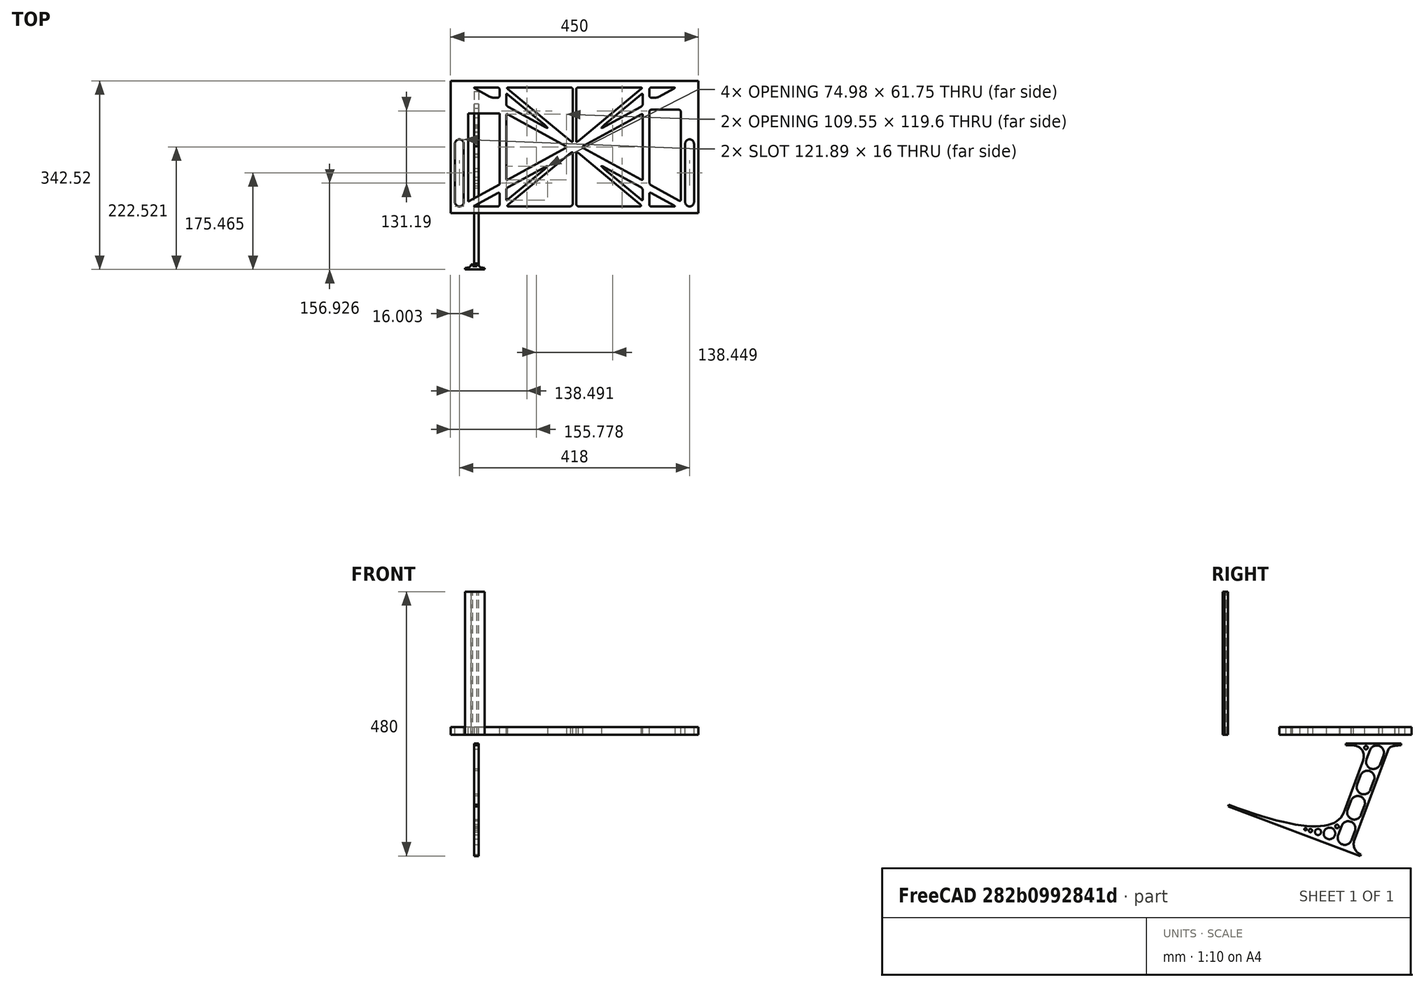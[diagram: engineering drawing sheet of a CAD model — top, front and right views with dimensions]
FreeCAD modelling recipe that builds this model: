
FCSTD DOCUMENT  (FreeCAD 0.19R0.19.2)
Label: laptopStand128FCStd
License: All rights reserved
LicenseURL: http://en.wikipedia.org/wiki/All_rights_reserved
objects: Sketcher::SketchObject×3, Part::Extrusion×3
note: 6 computed .brp shape members not serialized (recipe doc carries the construction recipe); baked Part::Feature solids carry a one-line shape summary decoded from their .brp

FEATURE [Sketcher::SketchObject] Sketch
  FullyConstrained = true
  sketch-geometry (353):
    g0: LineSegment StartX=-10.9272 StartY=-82.7794 StartZ=0 EndX=46.0728 EndY=-51.4823 EndZ=0
    g1: LineSegment StartX=-10.9272 StartY=76.4095 StartZ=0 EndX=-10.9272 EndY=-82.7794 EndZ=0
    g2: LineSegment StartX=46.0728 StartY=76.4095 StartZ=0 EndX=46.0728 EndY=-51.4823 EndZ=0
    g3: LineSegment StartX=-42.9272 StartY=136.221 StartZ=0 EndX=-42.9272 EndY=-103.779 EndZ=0
    g4: LineSegment StartX=407.073 StartY=136.221 StartZ=0 EndX=407.073 EndY=-103.779 EndZ=0
    g5: ArcOfCircle CenterX=-26.9272 CenterY=22.1087 CenterZ=0 NormalX=0 NormalY=0 NormalZ=1 AngleXU=0 Radius=8 StartAngle=1e-16 EndAngle=3.14159
    g6: ArcOfCircle CenterX=-26.9272 CenterY=-83.7794 CenterZ=0 NormalX=0 NormalY=0 NormalZ=1 AngleXU=0 Radius=8 StartAngle=3.14159 EndAngle=6.28319
    g7: LineSegment StartX=-34.9272 StartY=22.1087 StartZ=0 EndX=-34.9272 EndY=-83.7794 EndZ=0
    g8: LineSegment StartX=-18.9272 StartY=22.1087 StartZ=0 EndX=-18.9272 EndY=-83.7794 EndZ=0
    g9: ArcOfCircle CenterX=391.073 CenterY=22.1087 CenterZ=0 NormalX=0 NormalY=0 NormalZ=1 AngleXU=0 Radius=8 StartAngle=-4.4e-15 EndAngle=3.14159
    g10: LineSegment StartX=399.073 StartY=22.1087 StartZ=0 EndX=399.073 EndY=-83.7794 EndZ=0
    g11: LineSegment StartX=383.073 StartY=22.1087 StartZ=0 EndX=383.073 EndY=-83.7794 EndZ=0
    g12: ArcOfCircle CenterX=391.073 CenterY=-83.7794 CenterZ=0 NormalX=0 NormalY=0 NormalZ=1 AngleXU=0 Radius=8 StartAngle=3.14159 EndAngle=6.28319
    g13: Circle CenterX=175.022 CenterY=27.0628 CenterZ=0 NormalX=0 NormalY=0 NormalZ=1 AngleXU=0 Radius=1
    g14: Circle CenterX=179.022 CenterY=24.8665 CenterZ=0 NormalX=0 NormalY=0 NormalZ=1 AngleXU=0 Radius=1
    g15: Circle CenterX=179.022 CenterY=27.0628 CenterZ=0 NormalX=0 NormalY=0 NormalZ=1 AngleXU=0 Radius=1
    g16: BSplineCurve PolesCount=3 KnotsCount=2 Degree=2 IsPeriodic=0
    g17: GeomPoint X=175.022 Y=27.0628 Z=0
    g18: GeomPoint X=179.022 Y=27.0628 Z=0
    g19: Circle CenterX=189.124 CenterY=27.0628 CenterZ=0 NormalX=0 NormalY=0 NormalZ=1 AngleXU=0 Radius=1
    g20: Circle CenterX=185.124 CenterY=24.8665 CenterZ=0 NormalX=0 NormalY=0 NormalZ=1 AngleXU=0 Radius=1
    g21: Circle CenterX=185.124 CenterY=27.0628 CenterZ=0 NormalX=0 NormalY=0 NormalZ=1 AngleXU=0 Radius=1
    g22: BSplineCurve PolesCount=3 KnotsCount=2 Degree=2 IsPeriodic=0
    g23: GeomPoint X=189.124 Y=27.0628 Z=0
    g24: GeomPoint X=185.124 Y=27.0628 Z=0
    g25: Circle CenterX=175.022 CenterY=5.37834 CenterZ=0 NormalX=0 NormalY=0 NormalZ=1 AngleXU=0 Radius=1
    g26: Circle CenterX=179.022 CenterY=7.57463 CenterZ=0 NormalX=0 NormalY=0 NormalZ=1 AngleXU=0 Radius=1
    g27: Circle CenterX=179.022 CenterY=5.34704 CenterZ=0 NormalX=0 NormalY=0 NormalZ=1 AngleXU=0 Radius=1
    g28: BSplineCurve PolesCount=3 KnotsCount=2 Degree=2 IsPeriodic=0
    g29: GeomPoint X=175.022 Y=5.37834 Z=0
    g30: GeomPoint X=179.022 Y=5.34704 Z=0
    g31: Circle CenterX=189.124 CenterY=5.37834 CenterZ=0 NormalX=0 NormalY=0 NormalZ=1 AngleXU=0 Radius=1
    g32: Circle CenterX=185.124 CenterY=7.57463 CenterZ=0 NormalX=0 NormalY=0 NormalZ=1 AngleXU=0 Radius=1
    g33: Circle CenterX=185.124 CenterY=5.34704 CenterZ=0 NormalX=0 NormalY=0 NormalZ=1 AngleXU=0 Radius=1
    g34: BSplineCurve PolesCount=3 KnotsCount=2 Degree=2 IsPeriodic=0
    g35: GeomPoint X=189.124 Y=5.37834 Z=0
    g36: GeomPoint X=185.124 Y=5.34704 Z=0
    g37: Circle CenterX=165.871 CenterY=18.1458 CenterZ=0 NormalX=0 NormalY=0 NormalZ=1 AngleXU=0 Radius=1
    g38: Circle CenterX=169.377 CenterY=16.2206 CenterZ=0 NormalX=0 NormalY=0 NormalZ=1 AngleXU=0 Radius=1
    g39: Circle CenterX=165.871 CenterY=14.2954 CenterZ=0 NormalX=0 NormalY=0 NormalZ=1 AngleXU=0 Radius=1
    g40: BSplineCurve PolesCount=3 KnotsCount=2 Degree=2 IsPeriodic=0
    g41: GeomPoint X=165.871 Y=18.1458 Z=0
    g42: GeomPoint X=165.871 Y=14.2954 Z=0
    g43: Circle CenterX=198.275 CenterY=18.1458 CenterZ=0 NormalX=0 NormalY=0 NormalZ=1 AngleXU=0 Radius=1
    g44: Circle CenterX=194.768 CenterY=16.2206 CenterZ=0 NormalX=0 NormalY=0 NormalZ=1 AngleXU=0 Radius=1
    g45: Circle CenterX=198.275 CenterY=14.2954 CenterZ=0 NormalX=0 NormalY=0 NormalZ=1 AngleXU=0 Radius=1
    g46: BSplineCurve PolesCount=3 KnotsCount=2 Degree=2 IsPeriodic=0
    g47: GeomPoint X=198.275 Y=18.1458 Z=0
    g48: GeomPoint X=198.275 Y=14.2954 Z=0
    g49: LineSegment StartX=407.073 StartY=-103.779 StartZ=0 EndX=-42.9272 EndY=-103.779 EndZ=0
    g50: LineSegment StartX=407.073 StartY=136.221 StartZ=0 EndX=-42.9272 EndY=136.221 EndZ=0
    g51: LineSegment StartX=46.0728 StartY=76.4095 StartZ=0 EndX=-10.9272 EndY=76.4095 EndZ=0
    g52: Circle CenterX=125.607 CenterY=54.1951 CenterZ=0 NormalX=0 NormalY=0 NormalZ=1 AngleXU=0 Radius=1
    g53: Circle CenterX=139.632 CenterY=46.4944 CenterZ=0 NormalX=0 NormalY=0 NormalZ=1 AngleXU=0 Radius=1
    g54: Circle CenterX=127.326 CenterY=56.7187 CenterZ=0 NormalX=0 NormalY=0 NormalZ=1 AngleXU=0 Radius=1
    g55: BSplineCurve PolesCount=3 KnotsCount=2 Degree=2 IsPeriodic=0
    g56: GeomPoint X=125.607 Y=54.1951 Z=0
    g57: GeomPoint X=127.326 Y=56.7187 Z=0
    g58: Circle CenterX=236.821 CenterY=56.7187 CenterZ=0 NormalX=0 NormalY=0 NormalZ=1 AngleXU=0 Radius=1
    g59: Circle CenterX=224.513 CenterY=46.4944 CenterZ=0 NormalX=0 NormalY=0 NormalZ=1 AngleXU=0 Radius=1
    g60: Circle CenterX=238.538 CenterY=54.1951 CenterZ=0 NormalX=0 NormalY=0 NormalZ=1 AngleXU=0 Radius=1
    g61: BSplineCurve PolesCount=3 KnotsCount=2 Degree=2 IsPeriodic=0
    g62: GeomPoint X=236.821 Y=56.7187 Z=0
    g63: GeomPoint X=238.538 Y=54.1951 Z=0
    g64: Circle CenterX=238.538 CenterY=-21.7539 CenterZ=0 NormalX=0 NormalY=0 NormalZ=1 AngleXU=0 Radius=1
    g65: Circle CenterX=224.513 CenterY=-14.0532 CenterZ=0 NormalX=0 NormalY=0 NormalZ=1 AngleXU=0 Radius=1
    g66: Circle CenterX=236.821 CenterY=-24.2775 CenterZ=0 NormalX=0 NormalY=0 NormalZ=1 AngleXU=0 Radius=1
    g67: BSplineCurve PolesCount=3 KnotsCount=2 Degree=2 IsPeriodic=0
    g68: GeomPoint X=238.538 Y=-21.7539 Z=0
    g69: GeomPoint X=236.821 Y=-24.2775 Z=0
    g70: Circle CenterX=125.607 CenterY=-21.7539 CenterZ=0 NormalX=0 NormalY=0 NormalZ=1 AngleXU=0 Radius=1
    g71: Circle CenterX=139.632 CenterY=-14.0532 CenterZ=0 NormalX=0 NormalY=0 NormalZ=1 AngleXU=0 Radius=1
    g72: Circle CenterX=127.325 CenterY=-24.2775 CenterZ=0 NormalX=0 NormalY=0 NormalZ=1 AngleXU=0 Radius=1
    g73: BSplineCurve PolesCount=3 KnotsCount=2 Degree=2 IsPeriodic=0
    g74: GeomPoint X=125.607 Y=-21.7539 Z=0
    g75: GeomPoint X=127.325 Y=-24.2775 Z=0
    g76: Circle CenterX=302.996 CenterY=111.695 CenterZ=0 NormalX=0 NormalY=0 NormalZ=1 AngleXU=0 Radius=1
    g77: Circle CenterX=306.073 CenterY=114.251 CenterZ=0 NormalX=0 NormalY=0 NormalZ=1 AngleXU=0 Radius=1
    g78: Circle CenterX=306.073 CenterY=110.251 CenterZ=0 NormalX=0 NormalY=0 NormalZ=1 AngleXU=0 Radius=1
    g79: BSplineCurve PolesCount=3 KnotsCount=2 Degree=2 IsPeriodic=0
    g80: GeomPoint X=302.996 Y=111.695 Z=0
    g81: GeomPoint X=306.073 Y=110.251 Z=0
    g82: Circle CenterX=306.073 CenterY=95.2763 CenterZ=0 NormalX=0 NormalY=0 NormalZ=1 AngleXU=0 Radius=1
    g83: Circle CenterX=306.073 CenterY=91.2763 CenterZ=0 NormalX=0 NormalY=0 NormalZ=1 AngleXU=0 Radius=1
    g84: Circle CenterX=302.567 CenterY=89.3511 CenterZ=0 NormalX=0 NormalY=0 NormalZ=1 AngleXU=0 Radius=1
    g85: BSplineCurve PolesCount=3 KnotsCount=2 Degree=2 IsPeriodic=0
    g86: GeomPoint X=306.073 Y=95.2763 Z=0
    g87: GeomPoint X=302.567 Y=89.3511 Z=0
    g88: LineSegment StartX=306.073 StartY=110.251 StartZ=0 EndX=306.073 EndY=95.2763 EndZ=0
    g89: LineSegment StartX=302.996 StartY=111.695 StartZ=0 EndX=236.821 EndY=56.7187 EndZ=0
    g90: LineSegment StartX=238.538 StartY=54.1951 StartZ=0 EndX=302.567 EndY=89.3511 EndZ=0
    g91: Circle CenterX=61.1496 CenterY=111.695 CenterZ=0 NormalX=0 NormalY=0 NormalZ=1 AngleXU=0 Radius=1
    g92: Circle CenterX=58.0728 CenterY=114.251 CenterZ=0 NormalX=0 NormalY=0 NormalZ=1 AngleXU=0 Radius=1
    g93: Circle CenterX=58.0728 CenterY=110.251 CenterZ=0 NormalX=0 NormalY=0 NormalZ=1 AngleXU=0 Radius=1
    g94: BSplineCurve PolesCount=3 KnotsCount=2 Degree=2 IsPeriodic=0
    g95: GeomPoint X=61.1496 Y=111.695 Z=0
    g96: GeomPoint X=58.0728 Y=110.251 Z=0
    g97: Circle CenterX=61.5791 CenterY=89.3511 CenterZ=0 NormalX=0 NormalY=0 NormalZ=1 AngleXU=0 Radius=1
    g98: Circle CenterX=58.0728 CenterY=91.2763 CenterZ=0 NormalX=0 NormalY=0 NormalZ=1 AngleXU=0 Radius=1
    g99: Circle CenterX=58.0728 CenterY=95.2763 CenterZ=0 NormalX=0 NormalY=0 NormalZ=1 AngleXU=0 Radius=1
    g100: BSplineCurve PolesCount=3 KnotsCount=2 Degree=2 IsPeriodic=0
    g101: GeomPoint X=61.5791 Y=89.3511 Z=0
    g102: GeomPoint X=58.0728 Y=95.2763 Z=0
    g103: LineSegment StartX=58.0728 StartY=110.251 StartZ=0 EndX=58.0728 EndY=95.2763 EndZ=0
    g104: LineSegment StartX=61.1496 StartY=111.695 StartZ=0 EndX=127.326 EndY=56.7187 EndZ=0
    g105: LineSegment StartX=125.607 StartY=54.1951 StartZ=0 EndX=61.5791 EndY=89.3511 EndZ=0
    g106: Circle CenterX=61.5791 CenterY=-56.9099 CenterZ=0 NormalX=0 NormalY=0 NormalZ=1 AngleXU=0 Radius=1
    g107: Circle CenterX=58.0728 CenterY=-58.8351 CenterZ=0 NormalX=0 NormalY=0 NormalZ=1 AngleXU=0 Radius=1
    g108: Circle CenterX=58.0728 CenterY=-62.8351 CenterZ=0 NormalX=0 NormalY=0 NormalZ=1 AngleXU=0 Radius=1
    g109: BSplineCurve PolesCount=3 KnotsCount=2 Degree=2 IsPeriodic=0
    g110: GeomPoint X=61.5791 Y=-56.9099 Z=0
    g111: GeomPoint X=58.0728 Y=-62.8351 Z=0
    g112: Circle CenterX=58.0728 CenterY=-77.8102 CenterZ=0 NormalX=0 NormalY=0 NormalZ=1 AngleXU=0 Radius=1
    g113: Circle CenterX=58.0728 CenterY=-81.8102 CenterZ=0 NormalX=0 NormalY=0 NormalZ=1 AngleXU=0 Radius=1
    g114: Circle CenterX=61.1496 CenterY=-79.2541 CenterZ=0 NormalX=0 NormalY=0 NormalZ=1 AngleXU=0 Radius=1
    g115: BSplineCurve PolesCount=3 KnotsCount=2 Degree=2 IsPeriodic=0
    g116: GeomPoint X=58.0728 Y=-77.8102 Z=0
    g117: GeomPoint X=61.1496 Y=-79.2541 Z=0
    g118: LineSegment StartX=58.0728 StartY=-62.8351 StartZ=0 EndX=58.0728 EndY=-77.8102 EndZ=0
    g119: LineSegment StartX=61.1496 StartY=-79.2541 StartZ=0 EndX=127.325 EndY=-24.2775 EndZ=0
    g120: LineSegment StartX=125.607 StartY=-21.7539 StartZ=0 EndX=61.5791 EndY=-56.9099 EndZ=0
    g121: Circle CenterX=302.567 CenterY=-56.9099 CenterZ=0 NormalX=0 NormalY=0 NormalZ=1 AngleXU=0 Radius=1
    g122: Circle CenterX=306.073 CenterY=-58.8351 CenterZ=0 NormalX=0 NormalY=0 NormalZ=1 AngleXU=0 Radius=1
    g123: Circle CenterX=306.073 CenterY=-62.8351 CenterZ=0 NormalX=0 NormalY=0 NormalZ=1 AngleXU=0 Radius=1
    g124: BSplineCurve PolesCount=3 KnotsCount=2 Degree=2 IsPeriodic=0
    g125: GeomPoint X=302.567 Y=-56.9099 Z=0
    g126: GeomPoint X=306.073 Y=-62.8351 Z=0
    g127: Circle CenterX=302.996 CenterY=-79.2541 CenterZ=0 NormalX=0 NormalY=0 NormalZ=1 AngleXU=0 Radius=1
    g128: Circle CenterX=306.073 CenterY=-81.8102 CenterZ=0 NormalX=0 NormalY=0 NormalZ=1 AngleXU=0 Radius=1
    g129: Circle CenterX=306.073 CenterY=-77.8102 CenterZ=0 NormalX=0 NormalY=0 NormalZ=1 AngleXU=0 Radius=1
    g130: BSplineCurve PolesCount=3 KnotsCount=2 Degree=2 IsPeriodic=0
    g131: GeomPoint X=302.996 Y=-79.2541 Z=0
    g132: GeomPoint X=306.073 Y=-77.8102 Z=0
    g133: LineSegment StartX=306.073 StartY=-62.8351 StartZ=0 EndX=306.073 EndY=-77.8102 EndZ=0
    g134: LineSegment StartX=302.996 StartY=-79.2541 StartZ=0 EndX=236.821 EndY=-24.2775 EndZ=0
    g135: LineSegment StartX=238.538 StartY=-21.7539 StartZ=0 EndX=302.567 EndY=-56.9099 EndZ=0
    g136: Circle CenterX=61.6457 CenterY=-88.8112 CenterZ=0 NormalX=0 NormalY=0 NormalZ=1 AngleXU=0 Radius=1
    g137: Circle CenterX=58.0728 CenterY=-91.7794 CenterZ=0 NormalX=0 NormalY=0 NormalZ=1 AngleXU=0 Radius=1
    g138: Circle CenterX=63.9135 CenterY=-91.7794 CenterZ=0 NormalX=0 NormalY=0 NormalZ=1 AngleXU=0 Radius=1
    g139: BSplineCurve PolesCount=3 KnotsCount=2 Degree=2 IsPeriodic=0
    g140: GeomPoint X=61.6457 Y=-88.8112 Z=0
    g141: GeomPoint X=63.9135 Y=-91.7794 Z=0
    g142: Circle CenterX=179.022 CenterY=-85.8163 CenterZ=0 NormalX=0 NormalY=0 NormalZ=1 AngleXU=0 Radius=1
    g143: Circle CenterX=179.022 CenterY=-91.7794 CenterZ=0 NormalX=0 NormalY=0 NormalZ=1 AngleXU=0 Radius=1
    g144: Circle CenterX=171.895 CenterY=-91.7794 CenterZ=0 NormalX=0 NormalY=0 NormalZ=1 AngleXU=0 Radius=1
    g145: BSplineCurve PolesCount=3 KnotsCount=2 Degree=2 IsPeriodic=0
    g146: GeomPoint X=179.022 Y=-85.8163 Z=0
    g147: GeomPoint X=171.895 Y=-91.7794 Z=0
    g148: Circle CenterX=185.124 CenterY=-86.2028 CenterZ=0 NormalX=0 NormalY=0 NormalZ=1 AngleXU=0 Radius=1
    g149: Circle CenterX=185.124 CenterY=-91.7794 CenterZ=0 NormalX=0 NormalY=0 NormalZ=1 AngleXU=0 Radius=1
    g150: Circle CenterX=191.747 CenterY=-91.7794 CenterZ=0 NormalX=0 NormalY=0 NormalZ=1 AngleXU=0 Radius=1
    g151: BSplineCurve PolesCount=3 KnotsCount=2 Degree=2 IsPeriodic=0
    g152: GeomPoint X=185.124 Y=-86.2028 Z=0
    g153: GeomPoint X=191.747 Y=-91.7794 Z=0
    g154: Circle CenterX=299.888 CenterY=-86.6413 CenterZ=0 NormalX=0 NormalY=0 NormalZ=1 AngleXU=0 Radius=1
    g155: Circle CenterX=306.073 CenterY=-91.7794 CenterZ=0 NormalX=0 NormalY=0 NormalZ=1 AngleXU=0 Radius=1
    g156: Circle CenterX=298.776 CenterY=-91.7794 CenterZ=0 NormalX=0 NormalY=0 NormalZ=1 AngleXU=0 Radius=1
    g157: BSplineCurve PolesCount=3 KnotsCount=2 Degree=2 IsPeriodic=0
    g158: GeomPoint X=299.888 Y=-86.6413 Z=0
    g159: GeomPoint X=298.776 Y=-91.7794 Z=0
    g160: LineSegment StartX=189.124 StartY=5.37834 StartZ=0 EndX=299.888 EndY=-86.6413 EndZ=0
    g161: LineSegment StartX=298.776 StartY=-91.7794 StartZ=0 EndX=191.747 EndY=-91.7794 EndZ=0
    g162: LineSegment StartX=185.124 StartY=-86.2028 StartZ=0 EndX=185.124 EndY=5.34704 EndZ=0
    g163: LineSegment StartX=179.022 StartY=5.34704 StartZ=0 EndX=179.022 EndY=-85.8163 EndZ=0
    g164: LineSegment StartX=171.895 StartY=-91.7794 StartZ=0 EndX=63.9135 EndY=-91.7794 EndZ=0
    g165: LineSegment StartX=61.6457 StartY=-88.8112 StartZ=0 EndX=175.022 EndY=5.37834 EndZ=0
    g166: Circle CenterX=302.073 CenterY=124.221 CenterZ=0 NormalX=0 NormalY=0 NormalZ=1 AngleXU=0 Radius=1
    g167: Circle CenterX=306.073 CenterY=124.221 CenterZ=0 NormalX=0 NormalY=0 NormalZ=1 AngleXU=0 Radius=1
    g168: Circle CenterX=302.996 CenterY=121.665 CenterZ=0 NormalX=0 NormalY=0 NormalZ=1 AngleXU=0 Radius=1
    g169: BSplineCurve PolesCount=3 KnotsCount=2 Degree=2 IsPeriodic=0
    g170: GeomPoint X=302.073 Y=124.221 Z=0
    g171: GeomPoint X=302.996 Y=121.665 Z=0
    g172: Circle CenterX=189.124 CenterY=124.221 CenterZ=0 NormalX=0 NormalY=0 NormalZ=1 AngleXU=0 Radius=1
    g173: Circle CenterX=185.124 CenterY=124.221 CenterZ=0 NormalX=0 NormalY=0 NormalZ=1 AngleXU=0 Radius=1
    g174: Circle CenterX=185.124 CenterY=120.221 CenterZ=0 NormalX=0 NormalY=0 NormalZ=1 AngleXU=0 Radius=1
    g175: BSplineCurve PolesCount=3 KnotsCount=2 Degree=2 IsPeriodic=0
    g176: GeomPoint X=189.124 Y=124.221 Z=0
    g177: GeomPoint X=185.124 Y=120.221 Z=0
    g178: Circle CenterX=175.022 CenterY=124.221 CenterZ=0 NormalX=0 NormalY=0 NormalZ=1 AngleXU=0 Radius=1
    g179: Circle CenterX=179.022 CenterY=124.221 CenterZ=0 NormalX=0 NormalY=0 NormalZ=1 AngleXU=0 Radius=1
    g180: Circle CenterX=179.022 CenterY=120.221 CenterZ=0 NormalX=0 NormalY=0 NormalZ=1 AngleXU=0 Radius=1
    g181: BSplineCurve PolesCount=3 KnotsCount=2 Degree=2 IsPeriodic=0
    g182: GeomPoint X=175.022 Y=124.221 Z=0
    g183: GeomPoint X=179.022 Y=120.221 Z=0
    g184: Circle CenterX=62.0728 CenterY=124.221 CenterZ=0 NormalX=0 NormalY=0 NormalZ=1 AngleXU=0 Radius=1
    g185: Circle CenterX=58.0728 CenterY=124.221 CenterZ=0 NormalX=0 NormalY=0 NormalZ=1 AngleXU=0 Radius=1
    g186: Circle CenterX=61.1496 CenterY=121.665 CenterZ=0 NormalX=0 NormalY=0 NormalZ=1 AngleXU=0 Radius=1
    g187: BSplineCurve PolesCount=3 KnotsCount=2 Degree=2 IsPeriodic=0
    g188: GeomPoint X=62.0728 Y=124.221 Z=0
    g189: GeomPoint X=61.1496 Y=121.665 Z=0
    g190: LineSegment StartX=62.0728 StartY=124.221 StartZ=0 EndX=175.022 EndY=124.221 EndZ=0
    g191: LineSegment StartX=179.022 StartY=120.221 StartZ=0 EndX=179.022 EndY=27.0628 EndZ=0
    g192: LineSegment StartX=185.124 StartY=27.0628 StartZ=0 EndX=185.124 EndY=120.221 EndZ=0
    g193: LineSegment StartX=189.124 StartY=124.221 StartZ=0 EndX=302.073 EndY=124.221 EndZ=0
    g194: LineSegment StartX=302.996 StartY=121.665 StartZ=0 EndX=189.124 EndY=27.0628 EndZ=0
    g195: LineSegment StartX=175.022 StartY=27.0628 StartZ=0 EndX=61.1496 EndY=121.665 EndZ=0
    g196: Circle CenterX=61.5791 CenterY=75.4095 CenterZ=0 NormalX=0 NormalY=0 NormalZ=1 AngleXU=0 Radius=1
    g197: Circle CenterX=58.0728 CenterY=77.3346 CenterZ=0 NormalX=0 NormalY=0 NormalZ=1 AngleXU=0 Radius=1
    g198: Circle CenterX=58.0728 CenterY=73.3346 CenterZ=0 NormalX=0 NormalY=0 NormalZ=1 AngleXU=0 Radius=1
    g199: BSplineCurve PolesCount=3 KnotsCount=2 Degree=2 IsPeriodic=0
    g200: GeomPoint X=61.5791 Y=75.4095 Z=0
    g201: GeomPoint X=58.0728 Y=73.3346 Z=0
    g202: Circle CenterX=58.0728 CenterY=-40.8935 CenterZ=0 NormalX=0 NormalY=0 NormalZ=1 AngleXU=0 Radius=1
    g203: Circle CenterX=58.0728 CenterY=-44.8935 CenterZ=0 NormalX=0 NormalY=0 NormalZ=1 AngleXU=0 Radius=1
    g204: Circle CenterX=61.5791 CenterY=-42.9683 CenterZ=0 NormalX=0 NormalY=0 NormalZ=1 AngleXU=0 Radius=1
    g205: BSplineCurve PolesCount=3 KnotsCount=2 Degree=2 IsPeriodic=0
    g206: GeomPoint X=58.0728 Y=-40.8935 Z=0
    g207: GeomPoint X=61.5791 Y=-42.9683 Z=0
    g208: LineSegment StartX=61.5791 StartY=-42.9683 StartZ=0 EndX=165.871 EndY=14.2954 EndZ=0
    g209: LineSegment StartX=165.871 StartY=18.1458 StartZ=0 EndX=61.5791 EndY=75.4095 EndZ=0
    g210: LineSegment StartX=58.0728 StartY=73.3346 StartZ=0 EndX=58.0728 EndY=-40.8935 EndZ=0
    g211: Circle CenterX=302.567 CenterY=-42.9683 CenterZ=0 NormalX=0 NormalY=0 NormalZ=1 AngleXU=0 Radius=1
    g212: Circle CenterX=306.073 CenterY=-44.8935 CenterZ=0 NormalX=0 NormalY=0 NormalZ=1 AngleXU=0 Radius=1
    g213: Circle CenterX=306.073 CenterY=-40.8935 CenterZ=0 NormalX=0 NormalY=0 NormalZ=1 AngleXU=0 Radius=1
    g214: BSplineCurve PolesCount=3 KnotsCount=2 Degree=2 IsPeriodic=0
    g215: GeomPoint X=302.567 Y=-42.9683 Z=0
    g216: GeomPoint X=306.073 Y=-40.8935 Z=0
    g217: Circle CenterX=306.073 CenterY=73.3346 CenterZ=0 NormalX=0 NormalY=0 NormalZ=1 AngleXU=0 Radius=1
    g218: Circle CenterX=306.073 CenterY=77.3346 CenterZ=0 NormalX=0 NormalY=0 NormalZ=1 AngleXU=0 Radius=1
    g219: Circle CenterX=302.567 CenterY=75.4095 CenterZ=0 NormalX=0 NormalY=0 NormalZ=1 AngleXU=0 Radius=1
    g220: BSplineCurve PolesCount=3 KnotsCount=2 Degree=2 IsPeriodic=0
    g221: GeomPoint X=306.073 Y=73.3346 Z=0
    g222: GeomPoint X=302.567 Y=75.4095 Z=0
    g223: LineSegment StartX=302.567 StartY=-42.9683 StartZ=0 EndX=198.275 EndY=14.2954 EndZ=0
    g224: LineSegment StartX=198.275 StartY=18.1458 StartZ=0 EndX=302.567 EndY=75.4095 EndZ=0
    g225: LineSegment StartX=306.073 StartY=73.3346 StartZ=0 EndX=306.073 EndY=-40.8935 EndZ=0
    g226: LineSegment StartX=322.073 StartY=105.865 StartZ=0 EndX=328.643 EndY=105.865 EndZ=0
    g227: LineSegment StartX=318.073 StartY=120.221 StartZ=0 EndX=318.073 EndY=109.865 EndZ=0
    g228: LineSegment StartX=336.157 StartY=107.779 StartZ=0 EndX=362.567 EndY=122.294 EndZ=0
    g229: Circle CenterX=362.073 CenterY=124.221 CenterZ=0 NormalX=0 NormalY=0 NormalZ=1 AngleXU=0 Radius=1
    g230: Circle CenterX=366.073 CenterY=124.221 CenterZ=0 NormalX=0 NormalY=0 NormalZ=1 AngleXU=0 Radius=1
    g231: Circle CenterX=362.567 CenterY=122.294 CenterZ=0 NormalX=0 NormalY=0 NormalZ=1 AngleXU=0 Radius=1
    g232: BSplineCurve PolesCount=3 KnotsCount=2 Degree=2 IsPeriodic=0
    g233: GeomPoint X=362.073 Y=124.221 Z=0
    g234: GeomPoint X=362.567 Y=122.294 Z=0
    g235: Circle CenterX=322.073 CenterY=124.221 CenterZ=0 NormalX=0 NormalY=0 NormalZ=1 AngleXU=0 Radius=1
    g236: Circle CenterX=318.073 CenterY=124.221 CenterZ=0 NormalX=0 NormalY=0 NormalZ=1 AngleXU=0 Radius=1
    g237: Circle CenterX=318.073 CenterY=120.221 CenterZ=0 NormalX=0 NormalY=0 NormalZ=1 AngleXU=0 Radius=1
    g238: BSplineCurve PolesCount=3 KnotsCount=2 Degree=2 IsPeriodic=0
    g239: GeomPoint X=322.073 Y=124.221 Z=0
    g240: GeomPoint X=318.073 Y=120.221 Z=0
    g241: Circle CenterX=322.073 CenterY=105.865 CenterZ=0 NormalX=0 NormalY=0 NormalZ=1 AngleXU=0 Radius=1
    g242: Circle CenterX=318.073 CenterY=105.865 CenterZ=0 NormalX=0 NormalY=0 NormalZ=1 AngleXU=0 Radius=1
    g243: Circle CenterX=318.073 CenterY=109.865 CenterZ=0 NormalX=0 NormalY=0 NormalZ=1 AngleXU=0 Radius=1
    g244: BSplineCurve PolesCount=3 KnotsCount=2 Degree=2 IsPeriodic=0
    g245: GeomPoint X=322.073 Y=105.865 Z=0
    g246: GeomPoint X=318.073 Y=109.865 Z=0
    g247: Circle CenterX=336.157 CenterY=107.779 CenterZ=0 NormalX=0 NormalY=0 NormalZ=1 AngleXU=0 Radius=1
    g248: Circle CenterX=332.651 CenterY=105.853 CenterZ=0 NormalX=0 NormalY=0 NormalZ=1 AngleXU=0 Radius=1
    g249: Circle CenterX=328.643 CenterY=105.865 CenterZ=0 NormalX=0 NormalY=0 NormalZ=1 AngleXU=0 Radius=1
    g250: BSplineCurve PolesCount=3 KnotsCount=2 Degree=2 IsPeriodic=0
    g251: GeomPoint X=336.157 Y=107.779 Z=0
    g252: GeomPoint X=328.643 Y=105.865 Z=0
    g253: LineSegment StartX=322.073 StartY=124.221 StartZ=0 EndX=362.073 EndY=124.221 EndZ=0
    g254: Circle CenterX=371.567 CenterY=-80.8644 CenterZ=0 NormalX=0 NormalY=0 NormalZ=1 AngleXU=0 Radius=1
    g255: Circle CenterX=375.073 CenterY=-82.7896 CenterZ=0 NormalX=0 NormalY=0 NormalZ=1 AngleXU=0 Radius=1
    g256: Circle CenterX=375.073 CenterY=-78.7896 CenterZ=0 NormalX=0 NormalY=0 NormalZ=1 AngleXU=0 Radius=1
    g257: BSplineCurve PolesCount=3 KnotsCount=2 Degree=2 IsPeriodic=0
    g258: GeomPoint X=371.567 Y=-80.8644 Z=0
    g259: GeomPoint X=375.073 Y=-78.7896 Z=0
    g260: Circle CenterX=321.579 CenterY=-53.4075 CenterZ=0 NormalX=0 NormalY=0 NormalZ=1 AngleXU=0 Radius=1
    g261: Circle CenterX=318.073 CenterY=-51.4823 CenterZ=0 NormalX=0 NormalY=0 NormalZ=1 AngleXU=0 Radius=1
    g262: Circle CenterX=318.073 CenterY=-47.4823 CenterZ=0 NormalX=0 NormalY=0 NormalZ=1 AngleXU=0 Radius=1
    g263: BSplineCurve PolesCount=3 KnotsCount=2 Degree=2 IsPeriodic=0
    g264: GeomPoint X=321.579 Y=-53.4075 Z=0
    g265: GeomPoint X=318.073 Y=-47.4823 Z=0
    g266: Circle CenterX=318.073 CenterY=79.9235 CenterZ=0 NormalX=0 NormalY=0 NormalZ=1 AngleXU=0 Radius=1
    g267: Circle CenterX=318.073 CenterY=83.9235 CenterZ=0 NormalX=0 NormalY=0 NormalZ=1 AngleXU=0 Radius=1
    g268: Circle CenterX=322.073 CenterY=83.9235 CenterZ=0 NormalX=0 NormalY=0 NormalZ=1 AngleXU=0 Radius=1
    g269: BSplineCurve PolesCount=3 KnotsCount=2 Degree=2 IsPeriodic=0
    g270: GeomPoint X=318.073 Y=79.9235 Z=0
    g271: GeomPoint X=322.073 Y=83.9235 Z=0
    g272: Circle CenterX=375.073 CenterY=79.9235 CenterZ=0 NormalX=0 NormalY=0 NormalZ=1 AngleXU=0 Radius=1
    g273: Circle CenterX=375.073 CenterY=83.9235 CenterZ=0 NormalX=0 NormalY=0 NormalZ=1 AngleXU=0 Radius=1
    g274: Circle CenterX=371.073 CenterY=83.9235 CenterZ=0 NormalX=0 NormalY=0 NormalZ=1 AngleXU=0 Radius=1
    g275: BSplineCurve PolesCount=3 KnotsCount=2 Degree=2 IsPeriodic=0
    g276: GeomPoint X=375.073 Y=79.9235 Z=0
    g277: GeomPoint X=371.073 Y=83.9235 Z=0
    g278: LineSegment StartX=375.073 StartY=79.9235 StartZ=0 EndX=375.073 EndY=78.9235 EndZ=0
    g279: LineSegment StartX=371.567 StartY=-80.8644 StartZ=0 EndX=321.579 EndY=-53.4075 EndZ=0
    g280: LineSegment StartX=318.073 StartY=-47.4823 StartZ=0 EndX=318.073 EndY=76.4095 EndZ=0
    g281: Circle CenterX=321.579 CenterY=-67.3492 CenterZ=0 NormalX=0 NormalY=0 NormalZ=1 AngleXU=0 Radius=1
    g282: Circle CenterX=318.073 CenterY=-65.424 CenterZ=0 NormalX=0 NormalY=0 NormalZ=1 AngleXU=0 Radius=1
    g283: Circle CenterX=318.073 CenterY=-69.424 CenterZ=0 NormalX=0 NormalY=0 NormalZ=1 AngleXU=0 Radius=1
    g284: BSplineCurve PolesCount=3 KnotsCount=2 Degree=2 IsPeriodic=0
    g285: GeomPoint X=321.579 Y=-67.3492 Z=0
    g286: GeomPoint X=318.073 Y=-69.424 Z=0
    g287: Circle CenterX=362.567 CenterY=-89.8542 CenterZ=0 NormalX=0 NormalY=0 NormalZ=1 AngleXU=0 Radius=1
    g288: Circle CenterX=366.073 CenterY=-91.7794 CenterZ=0 NormalX=0 NormalY=0 NormalZ=1 AngleXU=0 Radius=1
    g289: Circle CenterX=362.073 CenterY=-91.7794 CenterZ=0 NormalX=0 NormalY=0 NormalZ=1 AngleXU=0 Radius=1
    g290: BSplineCurve PolesCount=3 KnotsCount=2 Degree=2 IsPeriodic=0
    g291: GeomPoint X=362.567 Y=-89.8542 Z=0
    g292: GeomPoint X=362.073 Y=-91.7794 Z=0
    g293: Circle CenterX=322.073 CenterY=-91.7794 CenterZ=0 NormalX=0 NormalY=0 NormalZ=1 AngleXU=0 Radius=1
    g294: Circle CenterX=318.073 CenterY=-91.7794 CenterZ=0 NormalX=0 NormalY=0 NormalZ=1 AngleXU=0 Radius=1
    g295: Circle CenterX=318.073 CenterY=-87.7794 CenterZ=0 NormalX=0 NormalY=0 NormalZ=1 AngleXU=0 Radius=1
    g296: BSplineCurve PolesCount=3 KnotsCount=2 Degree=2 IsPeriodic=0
    g297: GeomPoint X=322.073 Y=-91.7794 Z=0
    g298: GeomPoint X=318.073 Y=-87.7794 Z=0
    g299: LineSegment StartX=362.567 StartY=-89.8542 StartZ=0 EndX=321.579 EndY=-67.3492 EndZ=0
    g300: LineSegment StartX=318.073 StartY=-69.424 StartZ=0 EndX=318.073 EndY=-87.7794 EndZ=0
    g301: LineSegment StartX=322.073 StartY=-91.7794 StartZ=0 EndX=362.073 EndY=-91.7794 EndZ=0
    g302: Circle CenterX=2.07281 CenterY=124.221 CenterZ=0 NormalX=0 NormalY=0 NormalZ=1 AngleXU=0 Radius=1
    g303: Circle CenterX=1.57905 CenterY=122.295 CenterZ=0 NormalX=0 NormalY=0 NormalZ=1 AngleXU=0 Radius=1
    g304: BSplineCurve PolesCount=3 KnotsCount=2 Degree=2 IsPeriodic=0
    g305: GeomPoint X=2.07281 Y=124.221 Z=0
    g306: GeomPoint X=1.57905 Y=122.295 Z=0
    g307: Circle CenterX=42.0728 CenterY=124.221 CenterZ=0 NormalX=0 NormalY=0 NormalZ=1 AngleXU=0 Radius=1
    g308: Circle CenterX=46.0728 CenterY=124.221 CenterZ=0 NormalX=0 NormalY=0 NormalZ=1 AngleXU=0 Radius=1
    g309: Circle CenterX=46.0728 CenterY=120.221 CenterZ=0 NormalX=0 NormalY=0 NormalZ=1 AngleXU=0 Radius=1
    g310: BSplineCurve PolesCount=3 KnotsCount=2 Degree=2 IsPeriodic=0
    g311: GeomPoint X=42.0728 Y=124.221 Z=0
    g312: GeomPoint X=46.0728 Y=120.221 Z=0
    g313: Circle CenterX=46.0728 CenterY=109.865 CenterZ=0 NormalX=0 NormalY=0 NormalZ=1 AngleXU=0 Radius=1
    g314: Circle CenterX=46.0728 CenterY=105.865 CenterZ=0 NormalX=0 NormalY=0 NormalZ=1 AngleXU=0 Radius=1
    g315: Circle CenterX=42.0728 CenterY=105.865 CenterZ=0 NormalX=0 NormalY=0 NormalZ=1 AngleXU=0 Radius=1
    g316: BSplineCurve PolesCount=3 KnotsCount=2 Degree=2 IsPeriodic=0
    g317: GeomPoint X=46.0728 Y=109.865 Z=0
    g318: GeomPoint X=42.0728 Y=105.865 Z=0
    g319: Circle CenterX=35.5028 CenterY=105.865 CenterZ=0 NormalX=0 NormalY=0 NormalZ=1 AngleXU=0 Radius=1
    g320: Circle CenterX=31.5028 CenterY=105.865 CenterZ=0 NormalX=0 NormalY=0 NormalZ=1 AngleXU=0 Radius=1
    g321: Circle CenterX=27.9965 CenterY=107.79 CenterZ=0 NormalX=0 NormalY=0 NormalZ=1 AngleXU=0 Radius=1
    g322: BSplineCurve PolesCount=3 KnotsCount=2 Degree=2 IsPeriodic=0
    g323: GeomPoint X=35.5028 Y=105.865 Z=0
    g324: GeomPoint X=27.9965 Y=107.79 Z=0
    g325: LineSegment StartX=2.07281 StartY=124.221 StartZ=0 EndX=42.0728 EndY=124.221 EndZ=0
    g326: LineSegment StartX=46.0728 StartY=120.221 StartZ=0 EndX=46.0728 EndY=109.865 EndZ=0
    g327: LineSegment StartX=42.0728 StartY=105.865 StartZ=0 EndX=35.5028 EndY=105.865 EndZ=0
    g328: LineSegment StartX=27.9965 StartY=107.79 StartZ=0 EndX=1.57905 EndY=122.295 EndZ=0
    g329: Circle CenterX=42.5666 CenterY=-67.3492 CenterZ=0 NormalX=0 NormalY=0 NormalZ=1 AngleXU=0 Radius=1
    g330: Circle CenterX=46.0728 CenterY=-65.424 CenterZ=0 NormalX=0 NormalY=0 NormalZ=1 AngleXU=0 Radius=1
    g331: Circle CenterX=46.0728 CenterY=-69.424 CenterZ=0 NormalX=0 NormalY=0 NormalZ=1 AngleXU=0 Radius=1
    g332: BSplineCurve PolesCount=3 KnotsCount=2 Degree=2 IsPeriodic=0
    g333: GeomPoint X=42.5666 Y=-67.3492 Z=0
    g334: GeomPoint X=46.0728 Y=-69.424 Z=0
    g335: Circle CenterX=46.0728 CenterY=-87.7794 CenterZ=0 NormalX=0 NormalY=0 NormalZ=1 AngleXU=0 Radius=1
    g336: Circle CenterX=46.0728 CenterY=-91.7794 CenterZ=0 NormalX=0 NormalY=0 NormalZ=1 AngleXU=0 Radius=1
    g337: Circle CenterX=42.0728 CenterY=-91.7794 CenterZ=0 NormalX=0 NormalY=0 NormalZ=1 AngleXU=0 Radius=1
    g338: BSplineCurve PolesCount=3 KnotsCount=2 Degree=2 IsPeriodic=0
    g339: GeomPoint X=46.0728 Y=-87.7794 Z=0
    g340: GeomPoint X=42.0728 Y=-91.7794 Z=0
    g341: Circle CenterX=2.07281 CenterY=-91.7794 CenterZ=0 NormalX=0 NormalY=0 NormalZ=1 AngleXU=0 Radius=1
    g342: Circle CenterX=-1.92719 CenterY=-91.7794 CenterZ=0 NormalX=0 NormalY=0 NormalZ=1 AngleXU=0 Radius=1
    g343: Circle CenterX=1.57905 CenterY=-89.8542 CenterZ=0 NormalX=0 NormalY=0 NormalZ=1 AngleXU=0 Radius=1
    g344: BSplineCurve PolesCount=3 KnotsCount=2 Degree=2 IsPeriodic=0
    g345: GeomPoint X=2.07281 Y=-91.7794 Z=0
    g346: GeomPoint X=1.57905 Y=-89.8542 Z=0
    g347: LineSegment StartX=2.07281 StartY=-91.7794 StartZ=0 EndX=42.0728 EndY=-91.7794 EndZ=0
    g348: LineSegment StartX=46.0728 StartY=-87.7794 StartZ=0 EndX=46.0728 EndY=-69.424 EndZ=0
    g349: LineSegment StartX=42.5666 StartY=-67.3492 StartZ=0 EndX=1.57905 EndY=-89.8542 EndZ=0
    g350: LineSegment StartX=318.073 StartY=76.4095 StartZ=0 EndX=375.073 EndY=76.4095 EndZ=0
    g351: LineSegment StartX=375.073 StartY=76.4095 StartZ=0 EndX=375.073 EndY=-78.7896 EndZ=0
    g352: LineSegment StartX=318.073 StartY=78.9235 StartZ=0 EndX=318.073 EndY=79.9235 EndZ=0
  constraints (586):
    c: Coincident(g0,g2)
    c: Block(g0)
    c: Block(g1)
    c: Vertical(g3)
    c: Vertical(g4)
    c: Block(g4)
    c: Block(g3)
    c: Tangent(g5,g8) = 1.5708
    c: Tangent(g5,g7) = -1.5708
    c: Tangent(g7,g6) = -1.5708
    c: Tangent(g8,g6) = 1.5708
    c: Vertical(g7)
    c: Equal(g5,g6)
    c: Block(g8)
    c: Block(g7)
    c: Tangent(g9,g10) = 1.5708
    c: Tangent(g10,g12) = 1.5708
    c: Equal(g9,g12)
    c: Coincident(g11,g9)
    c: Coincident(g11,g12)
    c: Block(g10)
    c: Block(g11)
    c: Weight(g13) = 1
    c: Equal(g13,g14)
    c: Equal(g13,g15)
    c: InternalAlignment(g13,g16)
    c: InternalAlignment(g14,g16)
    c: InternalAlignment(g15,g16)
    c: InternalAlignment(g17,g16)
    c: InternalAlignment(g18,g16)
    c: Weight(g19) = 1
    c: Equal(g19,g20)
    c: Equal(g19,g21)
    c: InternalAlignment(g19,g22)
    c: InternalAlignment(g20,g22)
    c: InternalAlignment(g21,g22)
    c: InternalAlignment(g23,g22)
    c: InternalAlignment(g24,g22)
    c: Block(g22)
    c: Block(g16)
    c: Weight(g25) = 1
    c: Equal(g25,g26)
    c: Equal(g25,g27)
    c: InternalAlignment(g25,g28)
    c: InternalAlignment(g26,g28)
    c: InternalAlignment(g27,g28)
    c: InternalAlignment(g29,g28)
    c: InternalAlignment(g30,g28)
    c: Weight(g31) = 1
    c: Equal(g31,g32)
    c: Equal(g31,g33)
    c: InternalAlignment(g31,g34)
    c: InternalAlignment(g32,g34)
    c: InternalAlignment(g33,g34)
    c: InternalAlignment(g35,g34)
    c: InternalAlignment(g36,g34)
    c: Block(g34)
    c: Block(g28)
    c: Weight(g37) = 1
    c: Equal(g37,g38)
    c: Equal(g37,g39)
    c: InternalAlignment(g37,g40)
    c: InternalAlignment(g38,g40)
    c: InternalAlignment(g39,g40)
    c: InternalAlignment(g41,g40)
    c: InternalAlignment(g42,g40)
    c: Weight(g43) = 1
    c: Equal(g43,g44)
    c: Equal(g43,g45)
    c: InternalAlignment(g43,g46)
    c: InternalAlignment(g44,g46)
    c: InternalAlignment(g45,g46)
    c: InternalAlignment(g47,g46)
    c: InternalAlignment(g48,g46)
    c: Block(g40)
    c: Block(g46)
    c: Coincident(g49,g4)
    c: Coincident(g49,g3)
    c: Horizontal(g49)
    c: Distance(g49) = 450
    c: Coincident(g50,g4)
    c: Coincident(g50,g3)
    c: Horizontal(g50)
    c: Horizontal(g51)
    c: Coincident(g2,g51)
    c: Block(g51)
    c: Coincident(g1,g51)
    c: Weight(g52) = 1
    c: Equal(g52,g53)
    c: Equal(g52,g54)
    c: InternalAlignment(g52,g55)
    c: InternalAlignment(g53,g55)
    c: InternalAlignment(g54,g55)
    c: InternalAlignment(g56,g55)
    c: InternalAlignment(g57,g55)
    c: Block(g55)
    c: Weight(g58) = 1
    c: Equal(g58,g59)
    c: Equal(g58,g60)
    c: InternalAlignment(g58,g61)
    c: InternalAlignment(g59,g61)
    c: InternalAlignment(g60,g61)
    c: InternalAlignment(g62,g61)
    c: InternalAlignment(g63,g61)
    c: Block(g61)
    c: Weight(g64) = 1
    c: Equal(g64,g65)
    c: Equal(g64,g66)
    c: InternalAlignment(g64,g67)
    c: InternalAlignment(g65,g67)
    c: InternalAlignment(g66,g67)
    c: InternalAlignment(g68,g67)
    c: InternalAlignment(g69,g67)
    c: Block(g67)
    c: Weight(g70) = 1
    c: Equal(g70,g71)
    c: Equal(g70,g72)
    c: InternalAlignment(g70,g73)
    c: InternalAlignment(g71,g73)
    c: InternalAlignment(g72,g73)
    c: InternalAlignment(g74,g73)
    c: InternalAlignment(g75,g73)
    c: Block(g73)
    c: Weight(g76) = 1
    c: Equal(g76,g77)
    c: Equal(g76,g78)
    c: InternalAlignment(g76,g79)
    c: InternalAlignment(g77,g79)
    c: InternalAlignment(g78,g79)
    c: InternalAlignment(g80,g79)
    c: InternalAlignment(g81,g79)
    c: Weight(g82) = 1
    c: Equal(g82,g83)
    c: Equal(g82,g84)
    c: InternalAlignment(g82,g85)
    c: InternalAlignment(g83,g85)
    c: InternalAlignment(g84,g85)
    c: InternalAlignment(g86,g85)
    c: InternalAlignment(g87,g85)
    c: Block(g79)
    c: Block(g85)
    c: Coincident(g88,g79)
    c: Coincident(g88,g85)
    c: Vertical(g88)
    c: Coincident(g89,g79)
    c: Coincident(g89,g61)
    c: Coincident(g90,g61)
    c: Coincident(g90,g85)
    c: Weight(g91) = 1
    c: Equal(g91,g92)
    c: Equal(g91,g93)
    c: InternalAlignment(g91,g94)
    c: InternalAlignment(g92,g94)
    c: InternalAlignment(g93,g94)
    c: InternalAlignment(g95,g94)
    c: InternalAlignment(g96,g94)
    c: Weight(g97) = 1
    c: Equal(g97,g98)
    c: Equal(g97,g99)
    c: InternalAlignment(g97,g100)
    c: InternalAlignment(g98,g100)
    c: InternalAlignment(g99,g100)
    c: InternalAlignment(g101,g100)
    c: InternalAlignment(g102,g100)
    c: Block(g94)
    c: Block(g100)
    c: Coincident(g103,g94)
    c: Coincident(g103,g100)
    c: Vertical(g103)
    c: Coincident(g104,g94)
    c: Coincident(g104,g55)
    c: Coincident(g105,g55)
    c: Coincident(g105,g100)
    c: Weight(g106) = 1
    c: Equal(g106,g107)
    c: Equal(g106,g108)
    c: InternalAlignment(g106,g109)
    c: InternalAlignment(g107,g109)
    c: InternalAlignment(g108,g109)
    c: InternalAlignment(g110,g109)
    c: InternalAlignment(g111,g109)
    c: Weight(g112) = 1
    c: Equal(g112,g113)
    c: Equal(g112,g114)
    c: InternalAlignment(g112,g115)
    c: InternalAlignment(g113,g115)
    c: InternalAlignment(g114,g115)
    c: InternalAlignment(g116,g115)
    c: InternalAlignment(g117,g115)
    c: Block(g109)
    c: Block(g115)
    c: Coincident(g118,g109)
    c: Coincident(g118,g115)
    c: Vertical(g118)
    c: Coincident(g119,g115)
    c: Coincident(g119,g73)
    c: Coincident(g120,g73)
    c: Coincident(g120,g109)
    c: Weight(g121) = 1
    c: Equal(g121,g122)
    c: Equal(g121,g123)
    c: InternalAlignment(g121,g124)
    c: InternalAlignment(g122,g124)
    c: InternalAlignment(g123,g124)
    c: InternalAlignment(g125,g124)
    c: InternalAlignment(g126,g124)
    c: Weight(g127) = 1
    c: Equal(g127,g128)
    c: Equal(g127,g129)
    c: InternalAlignment(g127,g130)
    c: InternalAlignment(g128,g130)
    c: InternalAlignment(g129,g130)
    c: InternalAlignment(g131,g130)
    c: InternalAlignment(g132,g130)
    c: Block(g124)
    c: Block(g130)
    c: Coincident(g133,g124)
    c: Coincident(g133,g130)
    c: Vertical(g133)
    c: Coincident(g134,g130)
    c: Coincident(g134,g67)
    c: Coincident(g135,g67)
    c: Coincident(g135,g124)
    c: Weight(g136) = 1
    c: Equal(g136,g137)
    c: Equal(g136,g138)
    c: InternalAlignment(g136,g139)
    c: InternalAlignment(g137,g139)
    c: InternalAlignment(g138,g139)
    c: InternalAlignment(g140,g139)
    c: InternalAlignment(g141,g139)
    c: Weight(g142) = 1
    c: Equal(g142,g143)
    c: Equal(g142,g144)
    c: InternalAlignment(g142,g145)
    c: InternalAlignment(g143,g145)
    c: InternalAlignment(g144,g145)
    c: InternalAlignment(g146,g145)
    c: InternalAlignment(g147,g145)
    c: Weight(g148) = 1
    c: Equal(g148,g149)
    c: Equal(g148,g150)
    c: InternalAlignment(g148,g151)
    c: InternalAlignment(g149,g151)
    c: InternalAlignment(g150,g151)
    c: InternalAlignment(g152,g151)
    c: InternalAlignment(g153,g151)
    c: Weight(g154) = 1
    c: Equal(g154,g155)
    c: Equal(g154,g156)
    c: InternalAlignment(g154,g157)
    c: InternalAlignment(g155,g157)
    c: InternalAlignment(g156,g157)
    c: InternalAlignment(g158,g157)
    c: InternalAlignment(g159,g157)
    c: Block(g157)
    c: Block(g151)
    c: Block(g145)
    c: Block(g139)
    c: Coincident(g160,g34)
    c: Coincident(g160,g157)
    c: Coincident(g161,g157)
    c: Coincident(g161,g151)
    c: Horizontal(g161)
    c: Coincident(g162,g151)
    c: Coincident(g162,g34)
    c: Vertical(g162)
    c: Coincident(g163,g28)
    c: Coincident(g163,g145)
    c: Vertical(g163)
    c: Coincident(g164,g145)
    c: Coincident(g164,g139)
    c: Horizontal(g164)
    c: Coincident(g165,g139)
    c: Coincident(g165,g28)
    c: Weight(g166) = 1
    c: Equal(g166,g167)
    c: Equal(g166,g168)
    c: InternalAlignment(g166,g169)
    c: InternalAlignment(g167,g169)
    c: InternalAlignment(g168,g169)
    c: InternalAlignment(g170,g169)
    c: InternalAlignment(g171,g169)
    c: Weight(g172) = 1
    c: Equal(g172,g173)
    c: Equal(g172,g174)
    c: InternalAlignment(g172,g175)
    c: InternalAlignment(g173,g175)
    c: InternalAlignment(g174,g175)
    c: InternalAlignment(g176,g175)
    c: InternalAlignment(g177,g175)
    c: Weight(g178) = 1
    c: Equal(g178,g179)
    c: Equal(g178,g180)
    c: InternalAlignment(g178,g181)
    c: InternalAlignment(g179,g181)
    c: InternalAlignment(g180,g181)
    c: InternalAlignment(g182,g181)
    c: InternalAlignment(g183,g181)
    c: Weight(g184) = 1
    c: Equal(g184,g185)
    c: Equal(g184,g186)
    c: InternalAlignment(g184,g187)
    c: InternalAlignment(g185,g187)
    c: InternalAlignment(g186,g187)
    c: InternalAlignment(g188,g187)
    c: InternalAlignment(g189,g187)
    c: Block(g187)
    c: Block(g181)
    c: Block(g175)
    c: Block(g169)
    c: Coincident(g190,g187)
    c: Coincident(g190,g181)
    c: Horizontal(g190)
    c: Coincident(g191,g181)
    c: Coincident(g191,g16)
    c: Vertical(g191)
    c: Coincident(g192,g22)
    c: Coincident(g192,g175)
    c: Vertical(g192)
    c: Coincident(g193,g175)
    c: Coincident(g193,g169)
    c: Horizontal(g193)
    c: Coincident(g194,g169)
    c: Coincident(g194,g22)
    c: Coincident(g195,g16)
    c: Weight(g196) = 1
    c: Equal(g196,g197)
    c: Equal(g196,g198)
    c: InternalAlignment(g196,g199)
    c: InternalAlignment(g197,g199)
    c: InternalAlignment(g198,g199)
    c: InternalAlignment(g200,g199)
    c: InternalAlignment(g201,g199)
    c: Weight(g202) = 1
    c: Equal(g202,g203)
    c: Equal(g202,g204)
    c: InternalAlignment(g202,g205)
    c: InternalAlignment(g203,g205)
    c: InternalAlignment(g204,g205)
    c: InternalAlignment(g206,g205)
    c: InternalAlignment(g207,g205)
    c: Block(g205)
    c: Block(g199)
    c: Coincident(g208,g205)
    c: Coincident(g208,g40)
    c: Coincident(g209,g40)
    c: Coincident(g209,g199)
    c: Coincident(g210,g199)
    c: Coincident(g210,g205)
    c: Vertical(g210)
    c: Weight(g211) = 1
    c: Equal(g211,g212)
    c: Equal(g211,g213)
    c: InternalAlignment(g211,g214)
    c: InternalAlignment(g212,g214)
    c: InternalAlignment(g213,g214)
    c: InternalAlignment(g215,g214)
    c: InternalAlignment(g216,g214)
    c: Weight(g217) = 1
    c: Equal(g217,g218)
    c: Equal(g217,g219)
    c: InternalAlignment(g217,g220)
    c: InternalAlignment(g218,g220)
    c: InternalAlignment(g219,g220)
    c: InternalAlignment(g221,g220)
    c: InternalAlignment(g222,g220)
    c: Block(g220)
    c: Block(g214)
    c: Coincident(g223,g214)
    c: Coincident(g223,g46)
    c: Coincident(g224,g46)
    c: Coincident(g224,g220)
    c: Coincident(g225,g220)
    c: Coincident(g225,g214)
    c: Vertical(g225)
    c: Horizontal(g226)
    c: Block(g226)
    c: Vertical(g227)
    c: Block(g227)
    c: Block(g228)
    c: Weight(g229) = 1
    c: Equal(g229,g230)
    c: Equal(g229,g231)
    c: InternalAlignment(g229,g232)
    c: InternalAlignment(g230,g232)
    c: InternalAlignment(g231,g232)
    c: InternalAlignment(g233,g232)
    c: InternalAlignment(g234,g232)
    c: Weight(g235) = 1
    c: Equal(g235,g236)
    c: Equal(g235,g237)
    c: InternalAlignment(g235,g238)
    c: InternalAlignment(g236,g238)
    c: InternalAlignment(g237,g238)
    c: InternalAlignment(g239,g238)
    c: InternalAlignment(g240,g238)
    c: Weight(g241) = 1
    c: Equal(g241,g242)
    c: Equal(g241,g243)
    c: InternalAlignment(g241,g244)
    c: InternalAlignment(g242,g244)
    c: InternalAlignment(g243,g244)
    c: InternalAlignment(g245,g244)
    c: InternalAlignment(g246,g244)
    c: Weight(g247) = 1
    c: Equal(g247,g248)
    c: Equal(g247,g249)
    c: InternalAlignment(g247,g250)
    c: InternalAlignment(g248,g250)
    c: InternalAlignment(g249,g250)
    c: InternalAlignment(g251,g250)
    c: InternalAlignment(g252,g250)
    c: Block(g232)
    c: Block(g238)
    c: Block(g244)
    c: Block(g250)
    c: Coincident(g253,g238)
    c: Coincident(g253,g232)
    c: Horizontal(g253)
    c: Block(g195)
    c: Weight(g254) = 1
    c: Equal(g254,g255)
    c: Equal(g254,g256)
    c: InternalAlignment(g254,g257)
    c: InternalAlignment(g255,g257)
    c: InternalAlignment(g256,g257)
    c: InternalAlignment(g258,g257)
    c: InternalAlignment(g259,g257)
    c: Weight(g260) = 1
    c: Equal(g260,g261)
    c: Equal(g260,g262)
    c: InternalAlignment(g260,g263)
    c: InternalAlignment(g261,g263)
    c: InternalAlignment(g262,g263)
    c: InternalAlignment(g264,g263)
    c: InternalAlignment(g265,g263)
    c: Weight(g266) = 1
    c: Equal(g266,g267)
    c: Equal(g266,g268)
    c: InternalAlignment(g266,g269)
    c: InternalAlignment(g267,g269)
    c: InternalAlignment(g268,g269)
    c: InternalAlignment(g270,g269)
    c: InternalAlignment(g271,g269)
    c: Weight(g272) = 1
    c: Equal(g272,g273)
    c: Equal(g272,g274)
    c: InternalAlignment(g272,g275)
    c: InternalAlignment(g273,g275)
    c: InternalAlignment(g274,g275)
    c: InternalAlignment(g276,g275)
    c: InternalAlignment(g277,g275)
    c: Block(g257)
    c: Block(g263)
    c: Block(g269)
    c: Block(g275)
    c: Coincident(g278,g275)
    c: Coincident(g351,g257)
    c: Vertical(g278)
    c: Coincident(g279,g257)
    c: Coincident(g279,g263)
    c: Coincident(g280,g263)
    c: Coincident(g352,g269)
    c: Vertical(g280)
    c: Weight(g281) = 1
    c: Equal(g281,g282)
    c: Equal(g281,g283)
    c: InternalAlignment(g281,g284)
    c: InternalAlignment(g282,g284)
    c: InternalAlignment(g283,g284)
    c: InternalAlignment(g285,g284)
    c: InternalAlignment(g286,g284)
    c: Weight(g287) = 1
    c: Equal(g287,g288)
    c: Equal(g287,g289)
    c: InternalAlignment(g287,g290)
    c: InternalAlignment(g288,g290)
    c: InternalAlignment(g289,g290)
    c: InternalAlignment(g291,g290)
    c: InternalAlignment(g292,g290)
    c: Weight(g293) = 1
    c: Equal(g293,g294)
    c: Equal(g293,g295)
    c: InternalAlignment(g293,g296)
    c: InternalAlignment(g294,g296)
    c: InternalAlignment(g295,g296)
    c: InternalAlignment(g297,g296)
    c: InternalAlignment(g298,g296)
    c: Block(g296)
    c: Block(g290)
    c: Block(g284)
    c: Coincident(g299,g290)
    c: Coincident(g299,g284)
    c: Coincident(g300,g284)
    c: Coincident(g300,g296)
    c: Vertical(g300)
    c: Coincident(g301,g296)
    c: Coincident(g301,g290)
    c: Horizontal(g301)
    c: Weight(g302) = 1
    c: Equal(g302,g303)
    c: InternalAlignment(g302,g304)
    c: InternalAlignment(g303,g304)
    c: InternalAlignment(g305,g304)
    c: InternalAlignment(g306,g304)
    c: Weight(g307) = 1
    c: Equal(g307,g308)
    c: Equal(g307,g309)
    c: InternalAlignment(g307,g310)
    c: InternalAlignment(g308,g310)
    c: InternalAlignment(g309,g310)
    c: InternalAlignment(g311,g310)
    c: InternalAlignment(g312,g310)
    c: Weight(g313) = 1
    c: Equal(g313,g314)
    c: Equal(g313,g315)
    c: InternalAlignment(g313,g316)
    c: InternalAlignment(g314,g316)
    c: InternalAlignment(g315,g316)
    c: InternalAlignment(g317,g316)
    c: InternalAlignment(g318,g316)
    c: Equal(g319,g320)
    c: Equal(g319,g321)
    c: InternalAlignment(g319,g322)
    c: InternalAlignment(g320,g322)
    c: InternalAlignment(g321,g322)
    c: InternalAlignment(g323,g322)
    c: InternalAlignment(g324,g322)
    c: Block(g310)
    c: Block(g316)
    c: Block(g322)
    c: Block(g304)
    c: Coincident(g325,g304)
    c: Coincident(g325,g310)
    c: Horizontal(g325)
    c: Coincident(g326,g310)
    c: Coincident(g326,g316)
    c: Vertical(g326)
    c: Coincident(g327,g316)
    c: Coincident(g327,g322)
    c: Horizontal(g327)
    c: Coincident(g328,g322)
    c: Coincident(g328,g304)
    c: Weight(g329) = 1
    c: Equal(g329,g330)
    c: Equal(g329,g331)
    c: InternalAlignment(g329,g332)
    c: InternalAlignment(g330,g332)
    c: InternalAlignment(g331,g332)
    c: InternalAlignment(g333,g332)
    c: InternalAlignment(g334,g332)
    c: Weight(g335) = 1
    c: Equal(g335,g336)
    c: Equal(g335,g337)
    c: InternalAlignment(g335,g338)
    c: InternalAlignment(g336,g338)
    c: InternalAlignment(g337,g338)
    c: InternalAlignment(g339,g338)
    c: InternalAlignment(g340,g338)
    c: Weight(g341) = 1
    c: Equal(g341,g342)
    c: Equal(g341,g343)
    c: InternalAlignment(g341,g344)
    c: InternalAlignment(g342,g344)
    c: InternalAlignment(g343,g344)
    c: InternalAlignment(g345,g344)
    c: InternalAlignment(g346,g344)
    c: Block(g344)
    c: Block(g338)
    c: Block(g332)
    c: Coincident(g347,g344)
    c: Coincident(g347,g338)
    c: Horizontal(g347)
    c: Coincident(g348,g338)
    c: Coincident(g348,g332)
    c: Vertical(g348)
    c: Coincident(g349,g332)
    c: Coincident(g349,g344)
    c: Block(g350)
    c: PointOnObject(g278,g272)
    c: Coincident(g351,g350)
    c: Tangent(g278,g351)
    c: Coincident(g280,g350)
    c: PointOnObject(g352,g266)
    c: Tangent(g280,g352)
FEATURE [Sketcher::SketchObject] Sketch001
  FullyConstrained = true
  MapMode = 4
  Placement = pos=(0,0,0) rot=(0.57735,0.57735,0.57735;2.0944rad)
  Support = -> [Sketch]
  sketch-geometry (46):
    g0: BSplineCurve PolesCount=3 KnotsCount=2 Degree=2 IsPeriodic=0
    g1: ArcOfCircle CenterX=73.1223 CenterY=-32.291 CenterZ=0 NormalX=0 NormalY=0 NormalZ=1 AngleXU=0 Radius=13 StartAngle=5.92268 EndAngle=9.06428
    g2: ArcOfCircle CenterX=66.7816 CenterY=-49.1439 CenterZ=0 NormalX=0 NormalY=0 NormalZ=1 AngleXU=0 Radius=13 StartAngle=2.78068 EndAngle=5.92131
    g3: ArcOfCircle CenterX=55.9263 CenterY=-78.1807 CenterZ=0 NormalX=0 NormalY=0 NormalZ=1 AngleXU=0 Radius=13 StartAngle=5.92268 EndAngle=9.06428
    g4: ArcOfCircle CenterX=49.5884 CenterY=-95.0342 CenterZ=0 NormalX=0 NormalY=0 NormalZ=1 AngleXU=0 Radius=13 StartAngle=2.78068 EndAngle=5.92131
    g5: ArcOfCircle CenterX=38.7206 CenterY=-124.067 CenterZ=0 NormalX=0 NormalY=0 NormalZ=1 AngleXU=0 Radius=13 StartAngle=5.92268 EndAngle=9.06428
    g6: ArcOfCircle CenterX=32.3875 CenterY=-140.92 CenterZ=0 NormalX=0 NormalY=0 NormalZ=1 AngleXU=0 Radius=13 StartAngle=2.78068 EndAngle=5.92131
    g7: ArcOfCircle CenterX=21.4715 CenterY=-169.934 CenterZ=0 NormalX=0 NormalY=0 NormalZ=1 AngleXU=0 Radius=13 StartAngle=5.92268 EndAngle=9.06428
    g8: ArcOfCircle CenterX=15.1336 CenterY=-186.787 CenterZ=0 NormalX=0 NormalY=0 NormalZ=1 AngleXU=0 Radius=13 StartAngle=2.78068 EndAngle=5.92131
    g9-g12: Circle x4 (B-spline internal-alignment scaffolding for g13; pole/knot coordinates omitted)
    g13: BSplineCurve PolesCount=4 KnotsCount=2 Degree=3 IsPeriodic=0
    g14: GeomPoint X=28.8094 Y=-19.0875 Z=0
    g15: GeomPoint X=47.0443 Y=-50.4712 Z=0
    g16: Circle CenterX=53.5586 CenterY=-23.2695 CenterZ=0 NormalX=0 NormalY=0 NormalZ=1 AngleXU=0 Radius=3.24518
    g17: Circle CenterX=-195.441 CenterY=-127.082 CenterZ=0 NormalX=0 NormalY=0 NormalZ=1 AngleXU=0 Radius=1
    g18: Circle CenterX=-8.24091 CenterY=-197.481 CenterZ=0 NormalX=0 NormalY=0 NormalZ=1 AngleXU=0 Radius=1
    g19: Circle CenterX=12.8789 CenterY=-141.321 CenterZ=0 NormalX=0 NormalY=0 NormalZ=1 AngleXU=0 Radius=1
    g20: BSplineCurve PolesCount=3 KnotsCount=2 Degree=2 IsPeriodic=0
    g21: GeomPoint X=-195.441 Y=-127.082 Z=0
    g22: GeomPoint X=12.8789 Y=-141.321 Z=0
    g23: Circle CenterX=-12.8016 CenterY=-179.036 CenterZ=0 NormalX=0 NormalY=0 NormalZ=1 AngleXU=0 Radius=10.5072
    g24: Circle CenterX=0.933922 CenterY=-166.43 CenterZ=0 NormalX=0 NormalY=0 NormalZ=1 AngleXU=0 Radius=3.26661
    g25: Circle CenterX=-33.5518 CenterY=-176.44 CenterZ=0 NormalX=0 NormalY=0 NormalZ=1 AngleXU=0 Radius=5.64388
    g26: Circle CenterX=-47.2366 CenterY=-173.859 CenterZ=0 NormalX=0 NormalY=0 NormalZ=1 AngleXU=0 Radius=3.01653
    g27: Circle CenterX=-56.2595 CenterY=-171.456 CenterZ=0 NormalX=0 NormalY=0 NormalZ=1 AngleXU=0 Radius=2.12826
    g28: ArcOfCircle CenterX=51.2151 CenterY=-198.473 CenterZ=0 NormalX=0 NormalY=0 NormalZ=1 AngleXU=0 Radius=20 StartAngle=2.78189 EndAngle=4.35269
    g29: LineSegment StartX=32.4951 StartY=-191.433 StartZ=0 EndX=94.6578 EndY=-26.1352 EndZ=0
    g30: LineSegment StartX=43.1192 StartY=-220.001 StartZ=0 EndX=-196.497 EndY=-129.89 EndZ=0
    g31: LineSegment StartX=43.1192 StartY=-220.001 StartZ=0 EndX=44.1752 EndY=-217.193 EndZ=0
    g32: LineSegment StartX=117.223 StartY=-19.0875 StartZ=0 EndX=117.223 EndY=-16.0875 EndZ=0
    g33: LineSegment StartX=117.223 StartY=-16.0875 StartZ=0 EndX=17.2232 EndY=-16.0875 EndZ=0
    g34: LineSegment StartX=17.2232 StartY=-16.0875 StartZ=0 EndX=17.2232 EndY=-19.0875 EndZ=0
    g35: LineSegment StartX=28.8094 StartY=-19.0875 StartZ=0 EndX=17.2232 EndY=-19.0875 EndZ=0
    g36: LineSegment StartX=47.0443 StartY=-50.4712 StartZ=0 EndX=12.8789 EndY=-141.321 EndZ=0
    g37: LineSegment StartX=-195.441 StartY=-127.082 StartZ=0 EndX=-196.497 EndY=-129.89 EndZ=0
    g38: LineSegment StartX=85.2866 StartY=-36.8766 StartZ=0 EndX=78.9396 EndY=-53.7463 EndZ=0
    g39: LineSegment StartX=60.9579 StartY=-27.7053 StartZ=0 EndX=54.6191 EndY=-44.5532 EndZ=0
    g40: LineSegment StartX=68.0907 StartY=-82.7664 StartZ=0 EndX=61.7465 EndY=-99.6365 EndZ=0
    g41: LineSegment StartX=43.7619 StartY=-73.595 StartZ=0 EndX=37.426 EndY=-90.4435 EndZ=0
    g42: LineSegment StartX=50.885 StartY=-128.652 StartZ=0 EndX=44.5456 EndY=-145.522 EndZ=0
    g43: LineSegment StartX=26.5562 StartY=-119.481 StartZ=0 EndX=20.2251 EndY=-136.329 EndZ=0
    g44: LineSegment StartX=9.3071 StartY=-165.349 StartZ=0 EndX=2.97115 EndY=-182.197 EndZ=0
    g45: LineSegment StartX=33.6358 StartY=-174.52 StartZ=0 EndX=27.2917 EndY=-191.39 EndZ=0
  constraints (71):
    c: Block(g0)
    c: Block(g1)
    c: Block(g2)
    c: Block(g4)
    c: Block(g3)
    c: Block(g6)
    c: Block(g5)
    c: Block(g8)
    c: Block(g7)
    c: Weight(g9) = 1
    c: Equal(g9,g10)
    c: Equal(g9,g11)
    c: Equal(g9,g12)
    c: InternalAlignment(g9-g12 -> g13) x4
    c: InternalAlignment(g14,g13)
    c: InternalAlignment(g15,g13)
    c: Block(g16)
    c: Weight(g17) = 1
    c: Equal(g17,g18)
    c: Equal(g17,g19)
    c: InternalAlignment(g17,g20)
    c: InternalAlignment(g18,g20)
    c: InternalAlignment(g19,g20)
    c: InternalAlignment(g21,g20)
    c: InternalAlignment(g22,g20)
    c: Block(g20)
    c: Block(g23)
    c: Block(g24)
    c: Block(g25)
    c: Block(g26)
    c: Block(g27)
    c: Block(g28)
    c: Coincident(g29,g28)
    c: Coincident(g29,g0)
    c: Block(g13)
    c: Coincident(g31,g30)
    c: Coincident(g31,g28)
    c: Block(g31)
    c: Coincident(g32,g0)
    c: Vertical(g32)
    c: Coincident(g33,g32)
    c: Horizontal(g33)
    c: Coincident(g34,g33)
    c: Vertical(g34)
    c: Block(g33)
    c: Coincident(g35,g13)
    c: Coincident(g35,g34)
    c: Horizontal(g35)
    c: Coincident(g36,g13)
    c: Coincident(g36,g20)
    c: Coincident(g37,g20)
    c: Coincident(g37,g30)
    c: Block(g30)
    c: Coincident(g38,g1)
    c: Coincident(g38,g2)
    c: Coincident(g39,g1)
    c: Coincident(g39,g2)
    c: Coincident(g40,g3)
    c: Coincident(g40,g4)
    c: Coincident(g41,g3)
    c: Coincident(g41,g4)
    c: Coincident(g42,g5)
    c: Coincident(g42,g6)
    c: Coincident(g43,g5)
    c: Coincident(g43,g6)
    c: Coincident(g44,g7)
    c: Coincident(g44,g8)
    c: Coincident(g45,g7)
    c: Coincident(g45,g8)
    c: Distance(g30) = 256
    c: Distance(g33) = 100
FEATURE [Part::Extrusion] Extrude002
  Base = -> Sketch001
  Dir = (1,0,0)
  DirMode = 2
  FaceMakerClass = Part::FaceMakerBullseye
  LengthFwd = 8
  LengthRev = 0
  Solid = true
  Symmetric = false
FEATURE [Sketcher::SketchObject] Sketch002
  FullyConstrained = true
  sketch-geometry (20):
    g0: LineSegment StartX=-2.77179 StartY=-200.304 StartZ=0 EndX=5.22821 EndY=-200.304 EndZ=0
    g1: LineSegment StartX=5.22821 StartY=-200.304 StartZ=0 EndX=5.22821 EndY=-197.304 EndZ=0
    g2: LineSegment StartX=-2.77179 StartY=-200.304 StartZ=0 EndX=-2.77179 EndY=-197.304 EndZ=0
    g3: LineSegment StartX=5.22821 StartY=-197.304 StartZ=0 EndX=8.22821 EndY=-197.304 EndZ=0
    g4: LineSegment StartX=-2.77179 StartY=-197.304 StartZ=0 EndX=-5.77179 EndY=-197.304 EndZ=0
    g5: LineSegment StartX=19.2282 StartY=-203.304 StartZ=0 EndX=19.2282 EndY=-206.304 EndZ=0
    g6: LineSegment StartX=-16.7718 StartY=-203.304 StartZ=0 EndX=-16.7718 EndY=-206.304 EndZ=0
    g7: LineSegment StartX=-16.7718 StartY=-206.304 StartZ=0 EndX=19.2282 EndY=-206.304 EndZ=0
    g8: Circle CenterX=-16.7718 CenterY=-203.304 CenterZ=0 NormalX=0 NormalY=0 NormalZ=1 AngleXU=0 Radius=1
    g9: Circle CenterX=-5.77179 CenterY=-203.304 CenterZ=0 NormalX=0 NormalY=0 NormalZ=1 AngleXU=0 Radius=1
    g10: Circle CenterX=-5.77179 CenterY=-197.304 CenterZ=0 NormalX=0 NormalY=0 NormalZ=1 AngleXU=0 Radius=1
    g11: BSplineCurve PolesCount=3 KnotsCount=2 Degree=2 IsPeriodic=0
    g12: GeomPoint X=-16.7718 Y=-203.304 Z=0
    g13: GeomPoint X=-5.77179 Y=-197.304 Z=0
    g14: Circle CenterX=19.2282 CenterY=-203.304 CenterZ=0 NormalX=0 NormalY=0 NormalZ=1 AngleXU=0 Radius=1
    g15: Circle CenterX=8.22821 CenterY=-203.304 CenterZ=0 NormalX=0 NormalY=0 NormalZ=1 AngleXU=0 Radius=1
    g16: Circle CenterX=8.22821 CenterY=-197.304 CenterZ=0 NormalX=0 NormalY=0 NormalZ=1 AngleXU=0 Radius=1
    g17: BSplineCurve PolesCount=3 KnotsCount=2 Degree=2 IsPeriodic=0
    g18: GeomPoint X=19.2282 Y=-203.304 Z=0
    g19: GeomPoint X=8.22821 Y=-197.304 Z=0
  constraints (41):
    c: Horizontal(g0)
    c: Distance(g0) = 8
    c: Coincident(g1,g0)
    c: Vertical(g1)
    c: Distance(g1) = 3
    c: Coincident(g2,g0)
    c: Vertical(g2)
    c: Distance(g2) = 3
    c: Coincident(g3,g1)
    c: Horizontal(g3)
    c: Distance(g3) = 3
    c: Coincident(g4,g2)
    c: Horizontal(g4)
    c: Distance(g4) = 3
    c: Vertical(g5)
    c: Vertical(g6)
    c: Coincident(g7,g6)
    c: Coincident(g7,g5)
    c: Weight(g8) = 1
    c: Equal(g8,g9)
    c: Equal(g8,g10)
    c: Coincident(g11,g4)
    c: InternalAlignment(g8,g11)
    c: InternalAlignment(g9,g11)
    c: InternalAlignment(g10,g11)
    c: InternalAlignment(g12,g11)
    c: InternalAlignment(g13,g11)
    c: Coincident(g17,g5)
    c: Weight(g14) = 1
    c: Equal(g14,g15)
    c: Equal(g14,g16)
    c: Coincident(g17,g3)
    c: InternalAlignment(g14,g17)
    c: InternalAlignment(g15,g17)
    c: InternalAlignment(g16,g17)
    c: InternalAlignment(g18,g17)
    c: InternalAlignment(g19,g17)
    c: Block(g7)
    c: Block(g17)
    c: Block(g11)
    c: Block(g6)
FEATURE [Part::Extrusion] Extrude003
  Base = -> Sketch002
  Dir = (0,0,1)
  DirMode = 2
  FaceMakerClass = Part::FaceMakerBullseye
  LengthFwd = 260
  LengthRev = 0
  Solid = true
  Symmetric = false
FEATURE [Part::Extrusion] Extrude
  Base = -> Sketch
  Dir = (0,0,1)
  DirMode = 2
  FaceMakerClass = Part::FaceMakerBullseye
  LengthFwd = 14
  LengthRev = 0
  Solid = true
  Symmetric = false
